# Revit family: EURS_63_LF_FB_CoreLine Waterproof WT120C G2 L1500_PHI
name_source: partatom
category: Lighting Fixtures
revit_build: Autodesk Revit 2016 (Build: 20161004_0715(x64)
units: mm (PartAtom-declared; Revit-internal decimal feet)

## family parameters
Cut with Voids When Loaded = No
Host = Face
Light Source = No
Part Type = Normal
Room Calculation Point = No
Round Connector Dimension = Use Diameter
Shared = Yes

## types (1)
- EURS_63_LF_FB_CoreLine Waterproof WT120C G2 L1500_PHI
    12NC = 910500453337
    Apparent Load = 0 VA
    BIM Library - URL = http://www.lighting.philips.com
    Content version = 1.0
    Default Elevation = 0 mm  [stored 0 ft]
    Description = CoreLine Waterproof WT120C
    EOC = EOC CODE
    ETIM code = EC002892
    ETIM code URL = https://prod.etim-international.com
    Fixture code = 871829184047300
    Lamp = LAMP TYPE
    Lamp type = WT120C IES Data : L1500 1xLED34S_840
    Last IES update = 20-08-2019
    Manufacturer = Philips
    Model = WT120C G2 L1500
    Order code = 910500453337
    Product catalog - URL = http://www.lighting.philips.com
    Type Comments = Face Based
    URL = http://www.lighting.philips.com
    body height = 76 mm  [stored 0.249344 ft]
    bulb height = 27 mm
    ceiling thickness = 13 mm  [stored 0.0426509 ft]
    length = 1515 mm  [stored 4.97047 ft]
    light source = 2 mm  [stored 0.00656168 ft]
    suspension height = 9 mm  [stored 0.0295276 ft]
    width = 80 mm  [stored 0.262467 ft]
    width 02 = 1370 mm
    width/2 = 40 mm  [stored 0.131234 ft]

note: [stored X ft] marks values corroborated as IEEE doubles in the binary element streams (Revit-internal decimal feet)

## geometry (parser evidence)
native form markers: Sweep x8
no freeform markers — native parametric forms only
